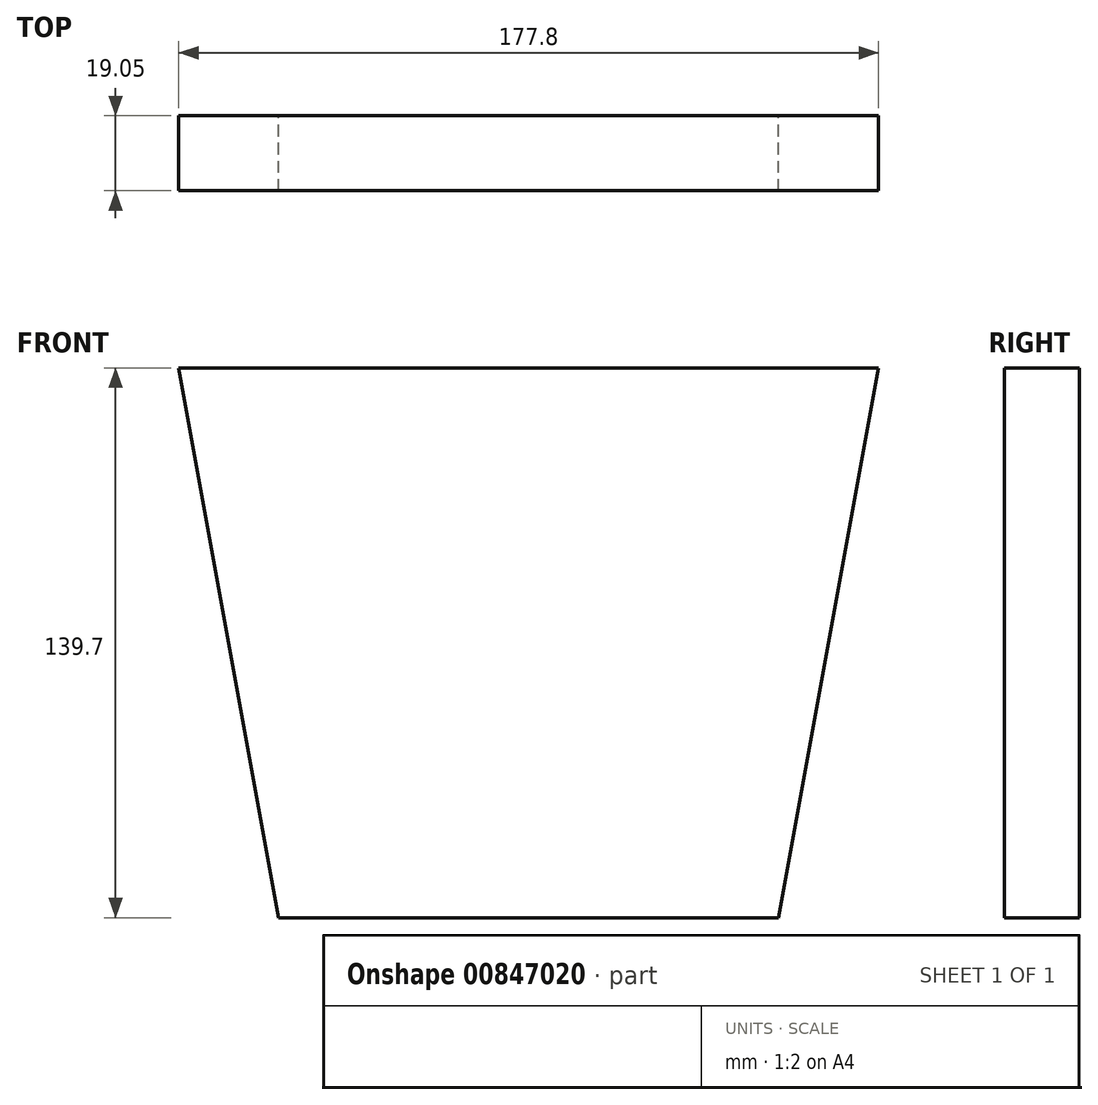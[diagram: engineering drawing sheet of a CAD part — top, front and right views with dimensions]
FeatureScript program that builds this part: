
annotation { "Feature Type Name" : "Feature", "Feature Type Description" : "" }
export const myFeature = defineFeature(function(context is Context, id is Id, definition is map)
    precondition{}
    {
        {
            var Q0;
            Q0=qCreatedBy(makeId("Front.planeOp"),FACE);
            var sketch = newSketch(context, id + "F0", { "sketchPlane" : qUnion([Q0])});
            skLineSegment(sketch, "E0.bottom", {"start": v(-223.18, 139.7) * mm, "end": v(-45.38, 139.7) * mm});
            skLineSegment(sketch, "E1", {"start": v(-223.18, 139.7) * mm, "end": v(-197.78, 0) * mm});
            skLineSegment(sketch, "E2", {"start": v(-45.38, 139.7) * mm, "end": v(-70.78, 0) * mm});
            skLineSegment(sketch, "E3", {"start": v(-70.78, 0) * mm, "end": v(-197.78, 0) * mm});
            skLineSegment(sketch, "E4", {"start": v(-223.18, 139.7) * mm, "end": v(-223.18, -87.47) * mm, "construction": true});
            skLineSegment(sketch, "E5", {"start": v(-45.38, 139.7) * mm, "end": v(-45.38, -94.17) * mm, "construction": true});
            skSolve(sketch);
        }
        {
            var Q0;
            Q0=makeQuery(id+"F0.imprint","IMPRINT",FACE,{"disambiguationData":[TD([[makeQuery(id+"F0.imprint","IMPRINT",EDGE,{"derivedFrom":sQuery(id+"F0.wireOp",EDGE,"E0.bottom")}),-1.0]])]});
            extrude(context, id + "F1", {"entities" : qUnion([Q0]), "depth" : 19.05 * mm, "offsetDistance" : 25.4 * mm});
        }
    });
